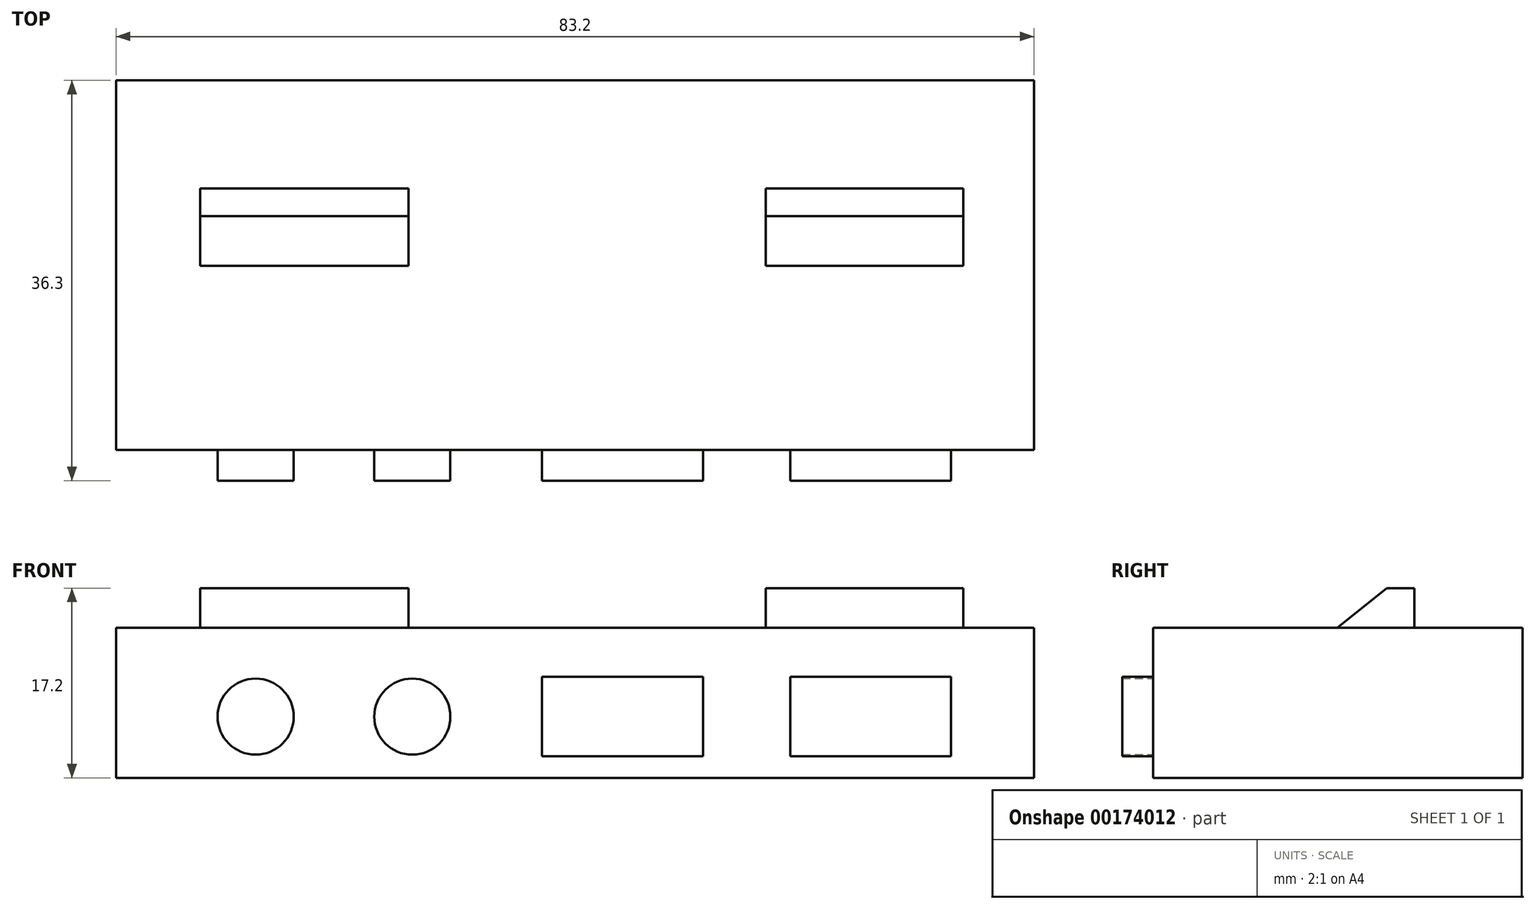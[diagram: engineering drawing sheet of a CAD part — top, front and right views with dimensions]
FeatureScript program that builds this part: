
annotation { "Feature Type Name" : "Feature", "Feature Type Description" : "" }
export const myFeature = defineFeature(function(context is Context, id is Id, definition is map)
    precondition{}
    {
        {
            var Q0;
            Q0=qCreatedBy(makeId("Front.planeOp"),FACE);
            var sketch = newSketch(context, id + "F0", { "sketchPlane" : qUnion([Q0])});
            skLineSegment(sketch, "E0.bottom", {"start": v(-41.6, 6.8) * mm, "end": v(41.6, 6.8) * mm});
            skLineSegment(sketch, "E0.top", {"start": v(-41.6, -6.8) * mm, "end": v(41.6, -6.8) * mm});
            skLineSegment(sketch, "E0.left", {"start": v(-41.6, 6.8) * mm, "end": v(-41.6, -6.8) * mm});
            skLineSegment(sketch, "E0.right", {"start": v(41.6, 6.8) * mm, "end": v(41.6, -6.8) * mm});
            skPoint(sketch, "E0.middle", {"position": v(0, 0) * mm});
            skSolve(sketch);
        }
        {
            var Q0;
            Q0 = qSketchRegion(id + "F0", true);
            extrude(context, id + "F1", {"entities" : qUnion([Q0]), "depth" : 33.5 * mm});
        }
        {
            var Q0;
            Q0=makeQuery(id+"F1.opExtrude","SWEPT_FACE",FACE,{"disambiguationData":[OSD([sQuery(id+"F0.wireOp",EDGE,"E0.left")])]});
            cPlane(context, id + "F2", {"entities" : qUnion([Q0]), "cplaneType" : CPlaneType.OFFSET, "offset" : 7.6 * mm, "oppositeDirection" : true, "width" : 150 * mm, "height" : 150 * mm});
        }
        {
            var Q0;
            Q0=qCreatedBy(id+"F2.planeOp",FACE);
            var sketch = newSketch(context, id + "F3", { "sketchPlane" : qUnion([Q0])});
            skLineSegment(sketch, "E1", {"start": v(9.8, 6.8) * mm, "end": v(9.8, 10.4) * mm});
            skLineSegment(sketch, "E2", {"start": v(9.8, 10.4) * mm, "end": v(12.3, 10.4) * mm});
            skLineSegment(sketch, "E3", {"start": v(12.3, 10.4) * mm, "end": v(16.8, 6.8) * mm});
            skLineSegment(sketch, "E4.0", {"start": v(16.8, 6.8) * mm, "end": v(9.8, 6.8) * mm});
            skPoint(sketch, "E5.orphan", {"position": v(0, 6.8) * mm});
            skPoint(sketch, "E6.orphan", {"position": v(33.5, 6.8) * mm});
            skSolve(sketch);
        }
        {
            var Q0;
            Q0 = qSketchRegion(id + "F3", true);
            extrude(context, id + "F4", {"entities" : qUnion([Q0]), "operationType" : NewBodyOperationType.ADD, "oppositeDirection" : true, "depth" : 69.2 * mm});
        }
        {
            var Q0;
            Q0=makeQuery(id+"F4.opExtrude","SWEPT_FACE",FACE,{"disambiguationData":[OSD([sQuery(id+"F3.wireOp",EDGE,"E1")])]});
            var sketch = newSketch(context, id + "F5", { "sketchPlane" : qUnion([Q0])});
            skLineSegment(sketch, "E7.bottom", {"start": v(-17.3, 10.4) * mm, "end": v(15.1, 10.4) * mm});
            skLineSegment(sketch, "E7.top", {"start": v(-17.3, 6.8) * mm, "end": v(15.1, 6.8) * mm});
            skLineSegment(sketch, "E7.left", {"start": v(-17.3, 10.4) * mm, "end": v(-17.3, 6.8) * mm});
            skLineSegment(sketch, "E7.right", {"start": v(15.1, 10.4) * mm, "end": v(15.1, 6.8) * mm});
            skSolve(sketch);
        }
        {
            var Q0;
            Q0 = qSketchRegion(id + "F5", true);
            var Q1;
            Q1=makeQuery(id+"F4.opExtrude","SWEPT_FACE",FACE,{"disambiguationData":[OSD([sQuery(id+"F3.wireOp",EDGE,"E3")])]});
            extrude(context, id + "F6", {"entities" : qUnion([Q0]), "operationType" : NewBodyOperationType.REMOVE, "endBound" : BoundingType.UP_TO_SURFACE, "oppositeDirection" : true, "endBoundEntityFace" : qUnion([Q1]), "depth" : 25 * mm});
        }
        {
            var Q0;
            Q0=makeQuery(id+"F1.opExtrude","CAP_FACE",FACE,{"disambiguationData":[OSD([sQuery(id+"F0.wireOp",EDGE,"E0.bottom"),sQuery(id+"F0.wireOp",EDGE,"E0.top"),sQuery(id+"F0.wireOp",EDGE,"E0.left"),sQuery(id+"F0.wireOp",EDGE,"E0.right")])],"isStart":false});
            var sketch = newSketch(context, id + "F7", { "sketchPlane" : qUnion([Q0])});
            skCircle(sketch, "E8", {"center": v(-28.95, -1.25) * mm, "radius": 3.45 * mm});
            skCircle(sketch, "E9", {"center": v(-14.75, -1.25) * mm, "radius": 3.45 * mm});
            skLineSegment(sketch, "E10.bottom", {"start": v(11.6, 2.35) * mm, "end": v(-3, 2.35) * mm});
            skLineSegment(sketch, "E10.top", {"start": v(11.6, -4.85) * mm, "end": v(-3, -4.85) * mm});
            skLineSegment(sketch, "E10.left", {"start": v(11.6, 2.35) * mm, "end": v(11.6, -4.85) * mm});
            skLineSegment(sketch, "E10.right", {"start": v(-3, 2.35) * mm, "end": v(-3, -4.85) * mm});
            skPoint(sketch, "E10.middle", {"position": v(4.3, -1.25) * mm});
            skLineSegment(sketch, "E11.bottom", {"start": v(34.1, 2.35) * mm, "end": v(19.5, 2.35) * mm});
            skLineSegment(sketch, "E11.top", {"start": v(34.1, -4.85) * mm, "end": v(19.5, -4.85) * mm});
            skLineSegment(sketch, "E11.left", {"start": v(34.1, 2.35) * mm, "end": v(34.1, -4.85) * mm});
            skLineSegment(sketch, "E11.right", {"start": v(19.5, 2.35) * mm, "end": v(19.5, -4.85) * mm});
            skPoint(sketch, "E11.middle", {"position": v(26.8, -1.25) * mm});
            skSolve(sketch);
        }
        {
            var Q0;
            Q0 = qSketchRegion(id + "F7", true);
            extrude(context, id + "F8", {"entities" : qUnion([Q0]), "operationType" : NewBodyOperationType.ADD, "depth" : 2.8 * mm});
        }
    });
